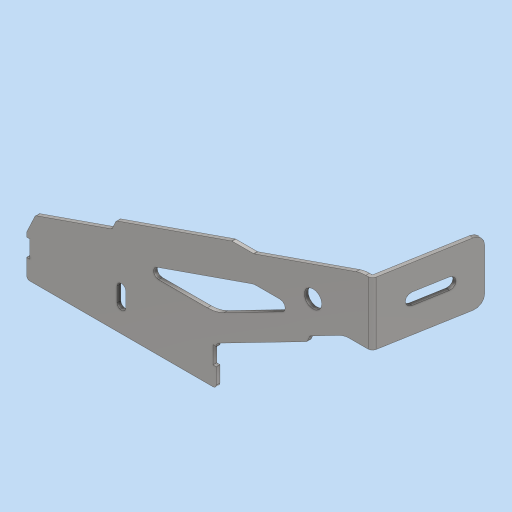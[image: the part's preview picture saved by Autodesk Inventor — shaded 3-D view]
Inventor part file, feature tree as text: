
AUTODESK INVENTOR PART (.ipt)
format: ipt  version: 2023 (Build 270158000, 158)  size: 577,536 bytes
history: native  units: mm
features: other x3, extrude x1, plane x1
ambient origin geometry x8: Origin, YZ Plane, XZ Plane, XY Plane, X Axis, Y Axis, Z Axis, Center Point
bodies: Body1 (feature_tree)
feature tree (5):
  other  "實體1"
  extrude  "擠出1"  Depth=130.0mm
  other  "折彎零件1"
  plane  "工作平面1"
  other  "定義1"
